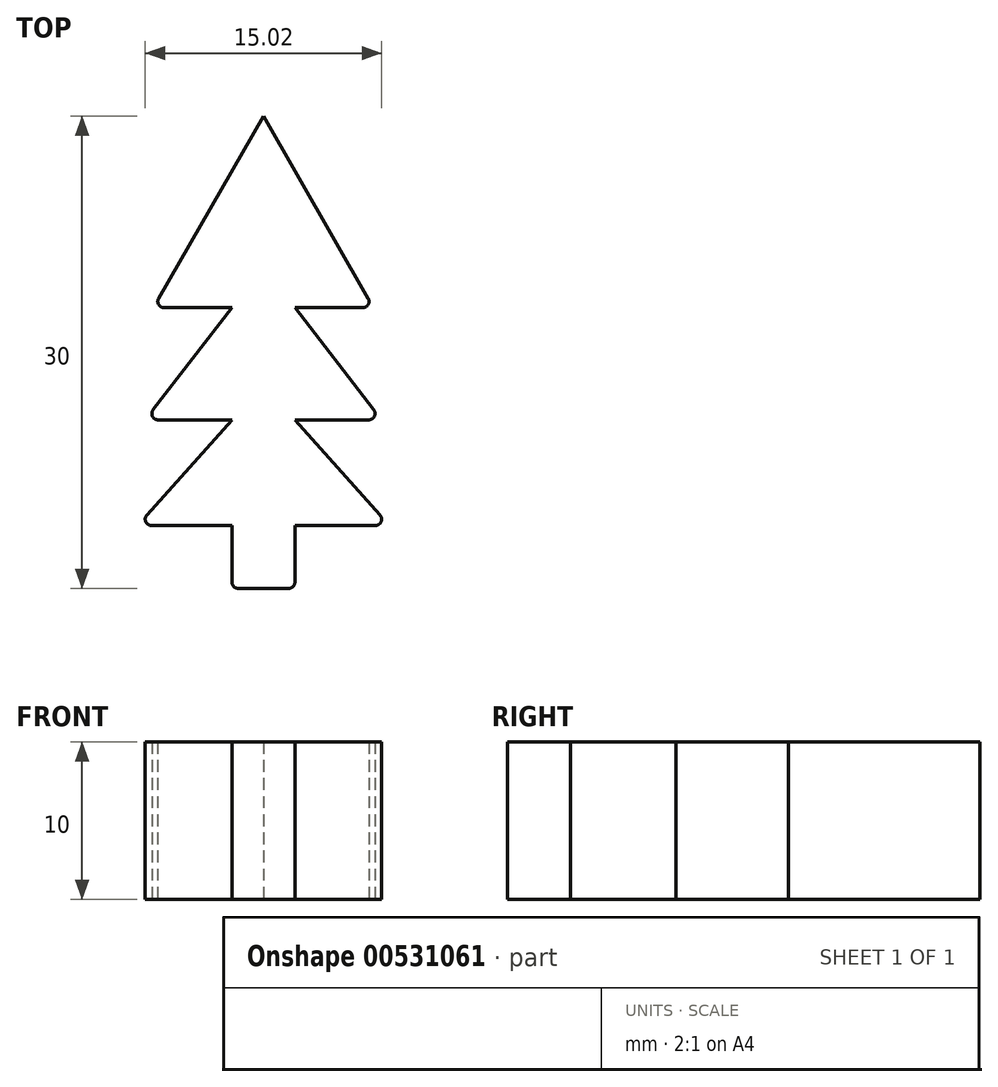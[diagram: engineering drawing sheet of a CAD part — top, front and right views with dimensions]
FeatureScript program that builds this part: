
annotation { "Feature Type Name" : "Feature", "Feature Type Description" : "" }
export const myFeature = defineFeature(function(context is Context, id is Id, definition is map)
    precondition{}
    {
        {
            var Q0;
            Q0=qCreatedBy(makeId("Top.planeOp"),FACE);
            var sketch = newSketch(context, id + "F0", { "sketchPlane" : qUnion([Q0])});
            skLineSegment(sketch, "E0", {"start": v(0, 17.97) * mm, "end": v(0, -12.03) * mm});
            skLineSegment(sketch, "E1", {"start": v(0, -12.03) * mm, "end": v(-1.6, -12.03) * mm});
            skLineSegment(sketch, "E2", {"start": v(-2, -11.63) * mm, "end": v(-2, -8.03) * mm});
            skLineSegment(sketch, "E3", {"start": v(-2, -8.03) * mm, "end": v(-7.1, -8.03) * mm});
            skLineSegment(sketch, "E4", {"start": v(-7.4, -7.37) * mm, "end": v(-2, -1.32) * mm});
            skLineSegment(sketch, "E5", {"start": v(-2, -1.32) * mm, "end": v(-6.69, -1.32) * mm});
            skLineSegment(sketch, "E6", {"start": v(-7, -0.68) * mm, "end": v(-2, 5.8) * mm});
            skLineSegment(sketch, "E7", {"start": v(-2, 5.8) * mm, "end": v(-6.3, 5.8) * mm});
            skLineSegment(sketch, "E8", {"start": v(-6.66, 6.4) * mm, "end": v(0, 17.97) * mm});
            skPoint(sketch, "E9.visualSharp", {"position": v(-7, 5.8) * mm});
            skArc(sketch, "E9.filletArc", {"start": v(-6.66, 6.4) * mm, "mid": v(-6.65, 6) * mm, "end": v(-6.3, 5.8) * mm});
            skPoint(sketch, "E10.visualSharp", {"position": v(-7.5, -1.32) * mm});
            skArc(sketch, "E10.filletArc", {"start": v(-7, -0.68) * mm, "mid": v(-7.04, -1.1) * mm, "end": v(-6.69, -1.32) * mm});
            skPoint(sketch, "E11.visualSharp", {"position": v(-8, -8.03) * mm});
            skArc(sketch, "E11.filletArc", {"start": v(-7.4, -7.37) * mm, "mid": v(-7.47, -7.8) * mm, "end": v(-7.1, -8.03) * mm});
            skPoint(sketch, "E12.MirrorCS.end.orphan", {"position": v(0, 17.97) * mm});
            skPoint(sketch, "E13.MirrorCS.start.orphan", {"position": v(0, -12.03) * mm});
            skLineSegment(sketch, "E14.MirrorCS", {"start": v(6.66, 6.4) * mm, "end": v(0, 17.97) * mm});
            skLineSegment(sketch, "E15.MirrorCS", {"start": v(2, 5.8) * mm, "end": v(6.3, 5.8) * mm});
            skArc(sketch, "E16.MirrorCS", {"start": v(6.66, 6.4) * mm, "mid": v(6.65, 6) * mm, "end": v(6.3, 5.8) * mm});
            skLineSegment(sketch, "E17.MirrorCS", {"start": v(7, -0.68) * mm, "end": v(2, 5.8) * mm});
            skArc(sketch, "E18.MirrorCS", {"start": v(7, -0.68) * mm, "mid": v(7.04, -1.1) * mm, "end": v(6.69, -1.32) * mm});
            skLineSegment(sketch, "E19.MirrorCS", {"start": v(2, -1.32) * mm, "end": v(6.69, -1.32) * mm});
            skLineSegment(sketch, "E20.MirrorCS", {"start": v(7.4, -7.37) * mm, "end": v(2, -1.32) * mm});
            skArc(sketch, "E21.MirrorCS", {"start": v(7.4, -7.37) * mm, "mid": v(7.47, -7.8) * mm, "end": v(7.1, -8.03) * mm});
            skLineSegment(sketch, "E22.MirrorCS", {"start": v(2, -8.03) * mm, "end": v(7.1, -8.03) * mm});
            skPoint(sketch, "E23.visualSharp", {"position": v(-2, -12.03) * mm});
            skArc(sketch, "E23.filletArc", {"start": v(-2, -11.63) * mm, "mid": v(-1.88, -11.92) * mm, "end": v(-1.6, -12.03) * mm});
            skLineSegment(sketch, "E24.MirrorCS", {"start": v(2, -11.63) * mm, "end": v(2, -8.03) * mm});
            skLineSegment(sketch, "E25.MirrorCS", {"start": v(0, -12.03) * mm, "end": v(1.6, -12.03) * mm});
            skArc(sketch, "E26.MirrorCS", {"start": v(2, -11.63) * mm, "mid": v(1.88, -11.92) * mm, "end": v(1.6, -12.03) * mm});
            skSolve(sketch);
        }
        {
            var Q0;
            Q0 = qSketchRegion(id + "F0", true);
            extrude(context, id + "F1", {"entities" : qUnion([Q0]), "depth" : 10 * mm, "offsetDistance" : 25 * mm});
        }
    });
